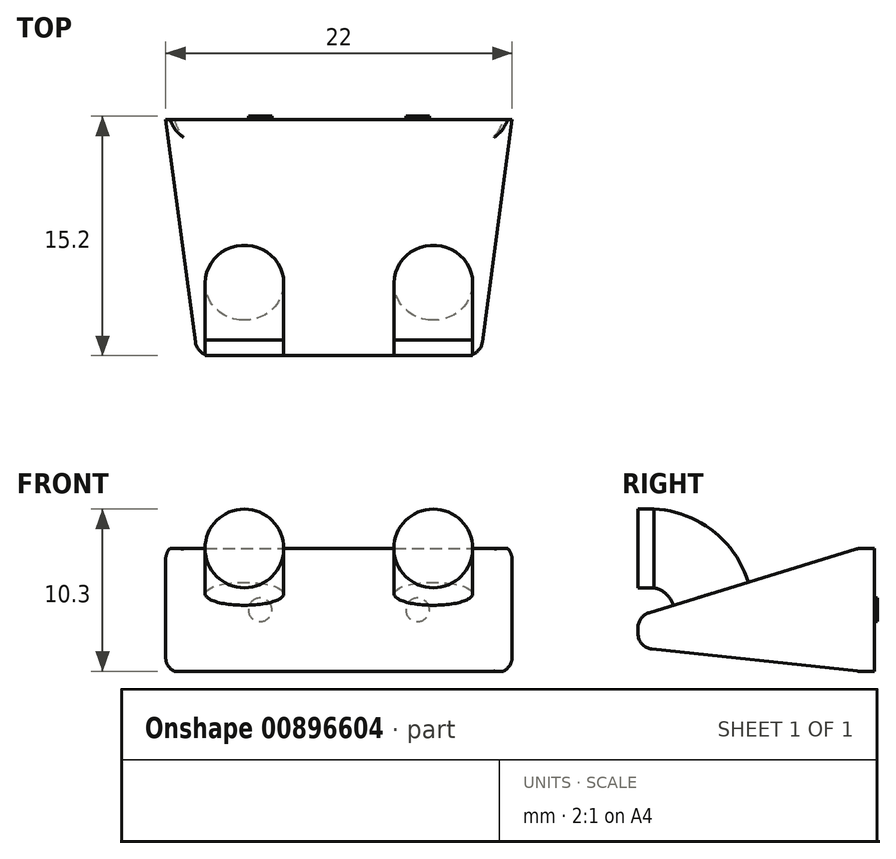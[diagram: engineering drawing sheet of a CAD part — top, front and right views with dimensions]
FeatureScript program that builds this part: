
annotation { "Feature Type Name" : "Feature", "Feature Type Description" : "" }
export const myFeature = defineFeature(function(context is Context, id is Id, definition is map)
    precondition{}
    {
        {
            var Q0;
            Q0=qCreatedBy(makeId("Front.planeOp"),FACE);
            var sketch = newSketch(context, id + "F0", { "sketchPlane" : qUnion([Q0])});
            skLineSegment(sketch, "E0.bottom", {"start": v(0, 0) * mm, "end": v(22, 0) * mm});
            skLineSegment(sketch, "E0.top", {"start": v(0, 7.8) * mm, "end": v(22, 7.8) * mm});
            skLineSegment(sketch, "E0.left", {"start": v(0, 0) * mm, "end": v(0, 7.8) * mm});
            skLineSegment(sketch, "E0.right", {"start": v(22, 0) * mm, "end": v(22, 7.8) * mm});
            skCircle(sketch, "E1", {"center": v(6, 3.9) * mm, "radius": 0.75 * mm});
            skCircle(sketch, "E2", {"center": v(16, 3.9) * mm, "radius": 0.75 * mm});
            skSolve(sketch);
        }
        {
            var Q0;
            Q0=makeQuery(id+"F0.imprint","IMPRINT",FACE,{"disambiguationData":[TD([[makeQuery(id+"F0.imprint","IMPRINT",EDGE,{"derivedFrom":sQuery(id+"F0.wireOp",EDGE,"E0.bottom")}),1.0]])]});
            var Q1;
            Q1=makeQuery(id+"F0.imprint","IMPRINT",FACE,{"disambiguationData":[TD([[makeQuery(id+"F0.imprint","IMPRINT",EDGE,{"derivedFrom":sQuery(id+"F0.wireOp",EDGE,"E2")}),1.0]])]});
            var Q2;
            Q2=makeQuery(id+"F0.imprint","IMPRINT",FACE,{"disambiguationData":[TD([[makeQuery(id+"F0.imprint","IMPRINT",EDGE,{"derivedFrom":sQuery(id+"F0.wireOp",EDGE,"E1")}),1.0]])]});
            extrude(context, id + "F1", {"entities" : qUnion([Q0, Q1, Q2]), "depth" : 1 * mm, "offsetDistance" : 25 * mm});
        }
        {
            var Q0;
            Q0=makeQuery(id+"F0.imprint","IMPRINT",FACE,{"disambiguationData":[TD([[makeQuery(id+"F0.imprint","IMPRINT",EDGE,{"derivedFrom":sQuery(id+"F0.wireOp",EDGE,"E2")}),1.0]])]});
            var Q1;
            Q1=makeQuery(id+"F0.imprint","IMPRINT",FACE,{"disambiguationData":[TD([[makeQuery(id+"F0.imprint","IMPRINT",EDGE,{"derivedFrom":sQuery(id+"F0.wireOp",EDGE,"E1")}),1.0]])]});
            extrude(context, id + "F2", {"entities" : qUnion([Q0, Q1]), "operationType" : NewBodyOperationType.ADD, "oppositeDirection" : true, "depth" : .2 * mm, "offsetDistance" : 25 * mm});
        }
        {
            var Q0;
            Q0=makeQuery(id+"F1.opExtrude","SWEPT_FACE",FACE,{"disambiguationData":[OSD([sQuery(id+"F0.wireOp",EDGE,"E0.right")])]});
            var sketch = newSketch(context, id + "F3", { "sketchPlane" : qUnion([Q0])});
            skLineSegment(sketch, "E3", {"start": v(-1, 0) * mm, "end": v(-15, 1.5) * mm});
            skLineSegment(sketch, "E4", {"start": v(-15, 1.5) * mm, "end": v(-15, 3.5) * mm});
            skLineSegment(sketch, "E5", {"start": v(-15, 3.5) * mm, "end": v(-1, 7.8) * mm});
            skSolve(sketch);
        }
        {
            var Q0;
            Q0 = qSketchRegion(id + "F3", true);
            var Q1;
            Q1=makeQuery(id+"F3.imprint","IMPRINT",FACE,{"disambiguationData":[TD([[makeQuery(id+"F3.imprint","IMPRINT",EDGE,{"derivedFrom":sQuery(id+"F3.wireOp",EDGE,"E3")}),-1.0]])]});
            extrude(context, id + "F4", {"entities" : qUnion([Q0, Q1]), "operationType" : NewBodyOperationType.ADD, "oppositeDirection" : true, "depth" : 22 * mm, "offsetDistance" : 25 * mm});
        }
        {
            var Q0;
            Q0=makeQuery(id+"F4.opExtrude","CAP_EDGE",EDGE,{"disambiguationData":[OSD([sQuery(id+"F3.wireOp",EDGE,"E4")])],"isStart":true});
            var Q1;
            Q1=makeQuery(id+"F4.opExtrude","CAP_EDGE",EDGE,{"disambiguationData":[OSD([sQuery(id+"F3.wireOp",EDGE,"E4")])],"isStart":false});
            chamfer(context, id + "F5", {"entities" : qUnion([Q0, Q1]), "chamferType" : ChamferType.TWO_OFFSETS, "width1" : 2 * mm, "oppositeDirection" : false, "width2" : 15 * mm, "tangentPropagation" : true});
        }
        {
            var Q0;
            Q0=makeQuery(id+"F4.opExtrude","SWEPT_EDGE",EDGE,{"disambiguationData":[OSD([sQuery(id+"F3.wireOp",EDGE,"E4"),sQuery(id+"F3.wireOp",EDGE,"E5")])]});
            var Q1;
            Q1=makeQuery(id+"F4.opExtrude","SWEPT_EDGE",EDGE,{"disambiguationData":[OSD([sQuery(id+"F3.wireOp",EDGE,"E3"),sQuery(id+"F3.wireOp",EDGE,"E4")])]});
            var Q2;
            Q2=makeQuery(id+"F5.opChamfer","BLEND_EDGE",EDGE,{"blendedFrom":[makeQuery(id+"F4.opExtrude","CAP_EDGE",EDGE,{"disambiguationData":[OSD([sQuery(id+"F3.wireOp",EDGE,"E4")])],"isStart":false}),makeQuery(id+"F4.opExtrude","SWEPT_FACE",FACE,{"disambiguationData":[OSD([sQuery(id+"F3.wireOp",EDGE,"E5")])]})],"blendedInto":[makeQuery(id+"F4.opExtrude","SWEPT_FACE",FACE,{"disambiguationData":[OSD([sQuery(id+"F3.wireOp",EDGE,"E5")])]})]});
            var Q3;
            Q3=makeQuery(id+"F5.opChamfer","BLEND_EDGE",EDGE,{"blendedFrom":[makeQuery(id+"F4.opExtrude","CAP_EDGE",EDGE,{"disambiguationData":[OSD([sQuery(id+"F3.wireOp",EDGE,"E4")])],"isStart":false}),makeQuery(id+"F4.opExtrude","SWEPT_FACE",FACE,{"disambiguationData":[OSD([sQuery(id+"F3.wireOp",EDGE,"E3")])]})],"blendedInto":[makeQuery(id+"F4.opExtrude","SWEPT_FACE",FACE,{"disambiguationData":[OSD([sQuery(id+"F3.wireOp",EDGE,"E3")])]})]});
            var Q4;
            Q4=makeQuery(id+"F5.opChamfer","BLEND_EDGE",EDGE,{"blendedFrom":[makeQuery(id+"F4.opExtrude","CAP_EDGE",EDGE,{"disambiguationData":[OSD([sQuery(id+"F3.wireOp",EDGE,"E4")])],"isStart":true}),makeQuery(id+"F4.opExtrude","SWEPT_FACE",FACE,{"disambiguationData":[OSD([sQuery(id+"F3.wireOp",EDGE,"E5")])]})],"blendedInto":[makeQuery(id+"F4.opExtrude","SWEPT_FACE",FACE,{"disambiguationData":[OSD([sQuery(id+"F3.wireOp",EDGE,"E5")])]})]});
            var Q5;
            Q5=makeQuery(id+"F5.opChamfer","BLEND_EDGE",EDGE,{"blendedFrom":[makeQuery(id+"F4.opExtrude","CAP_EDGE",EDGE,{"disambiguationData":[OSD([sQuery(id+"F3.wireOp",EDGE,"E4")])],"isStart":true}),makeQuery(id+"F4.opExtrude","SWEPT_FACE",FACE,{"disambiguationData":[OSD([sQuery(id+"F3.wireOp",EDGE,"E3")])]})],"blendedInto":[makeQuery(id+"F4.opExtrude","SWEPT_FACE",FACE,{"disambiguationData":[OSD([sQuery(id+"F3.wireOp",EDGE,"E3")])]})]});
            var Q6;
            {var subQ0=sQuery(id+"F3.wireOp",EDGE,"E4");Q6=makeQuery(id+"F5.opChamfer","BLEND_EDGE",EDGE,{"blendedFrom":[makeQuery(id+"F4.opExtrude","CAP_EDGE",EDGE,{"disambiguationData":[OSD([subQ0])],"isStart":true}),makeQuery(id+"F4.opExtrude","SWEPT_FACE",FACE,{"disambiguationData":[OSD([subQ0])]})],"blendedInto":[makeQuery(id+"F4.opExtrude","SWEPT_FACE",FACE,{"disambiguationData":[OSD([subQ0])]})]});}
            var Q7;
            {var subQ0=sQuery(id+"F3.wireOp",EDGE,"E4");Q7=makeQuery(id+"F5.opChamfer","BLEND_EDGE",EDGE,{"blendedFrom":[makeQuery(id+"F4.opExtrude","CAP_EDGE",EDGE,{"disambiguationData":[OSD([subQ0])],"isStart":false}),makeQuery(id+"F4.opExtrude","SWEPT_FACE",FACE,{"disambiguationData":[OSD([subQ0])]})],"blendedInto":[makeQuery(id+"F4.opExtrude","SWEPT_FACE",FACE,{"disambiguationData":[OSD([subQ0])]})]});}
            var Q8;
            {var subQ0=sQuery(id+"F0.wireOp",EDGE,"E0.bottom");Q8=makeQuery(id+"F4.boolean.opBoolean","MERGE",EDGE,{"derivedFrom":[makeQuery(id+"F1.opExtrude","CAP_EDGE",EDGE,{"disambiguationData":[OSD([subQ0])],"isStart":false}),makeQuery(id+"F4.opExtrude","SWEPT_EDGE",EDGE,{"disambiguationData":[OSD([subQ0,sQuery(id+"F0.wireOp",EDGE,"E0.right"),sQuery(id+"F3.wireOp",EDGE,"E3")])]})]});}
            var Q9;
            {var subQ0=sQuery(id+"F0.wireOp",EDGE,"E0.top");Q9=makeQuery(id+"F4.boolean.opBoolean","MERGE",EDGE,{"derivedFrom":[makeQuery(id+"F1.opExtrude","CAP_EDGE",EDGE,{"disambiguationData":[OSD([subQ0])],"isStart":false}),makeQuery(id+"F4.opExtrude","SWEPT_EDGE",EDGE,{"disambiguationData":[OSD([subQ0,sQuery(id+"F0.wireOp",EDGE,"E0.right"),sQuery(id+"F3.wireOp",EDGE,"E5")])]})]});}
            fillet(context, id + "F6", {"entities" : qUnion([Q0, Q1, Q2, Q3, Q4, Q5, Q6, Q7, Q8, Q9]), "radius" : 1 * mm, "tangentPropagation" : true, "allowEdgeOverflow" : false});
        }
        {
            var Q0;
            Q0=makeQuery(id+"F4.opExtrude","SWEPT_FACE",FACE,{"disambiguationData":[OSD([sQuery(id+"F3.wireOp",EDGE,"E4")])]});
            var sketch = newSketch(context, id + "F7", { "sketchPlane" : qUnion([Q0])});
            skCircle(sketch, "E6", {"center": v(17, 7.8) * mm, "radius": 2.5 * mm});
            skCircle(sketch, "E7", {"center": v(5, 7.8) * mm, "radius": 2.5 * mm});
            skSolve(sketch);
        }
        {
            var Q0;
            Q0=makeQuery(id+"F7.imprint","IMPRINT",FACE,{"disambiguationData":[TD([[makeQuery(id+"F7.imprint","IMPRINT",EDGE,{"derivedFrom":sQuery(id+"F7.wireOp",EDGE,"E6")}),1.0]])]});
            var Q1;
            Q1=makeQuery(id+"F7.imprint","IMPRINT",FACE,{"disambiguationData":[TD([[makeQuery(id+"F7.imprint","IMPRINT",EDGE,{"derivedFrom":sQuery(id+"F7.wireOp",EDGE,"E7")}),1.0]])]});
            extrude(context, id + "F8", {"entities" : qUnion([Q0, Q1]), "oppositeDirection" : true, "depth" : 1 * mm, "offsetDistance" : 25 * mm});
        }
        {
            var Q0;
            Q0=makeQuery(id+"F8.opExtrude","CAP_FACE",FACE,{"disambiguationData":[OSD([sQuery(id+"F7.wireOp",EDGE,"E7")])],"isStart":false});
            var Q1;
            Q1=makeQuery(id+"F8.opExtrude","CAP_FACE",FACE,{"disambiguationData":[OSD([sQuery(id+"F7.wireOp",EDGE,"E6")])],"isStart":false});
            var Q2;
            {var subQ0=sQuery(id+"F3.wireOp",EDGE,"E5");Q2=makeQuery(id+"F6.opFillet","BLEND_EDGE",EDGE,{"blendedFrom":[makeQuery(id+"F4.opExtrude","SWEPT_EDGE",EDGE,{"disambiguationData":[OSD([sQuery(id+"F3.wireOp",EDGE,"E4"),subQ0])]}),makeQuery(id+"F4.opExtrude","SWEPT_FACE",FACE,{"disambiguationData":[OSD([subQ0])]})],"blendedInto":[makeQuery(id+"F4.opExtrude","SWEPT_FACE",FACE,{"disambiguationData":[OSD([subQ0])]})]});}
            revolve(context, id + "F9", {"operationType" : NewBodyOperationType.ADD, "surfaceOperationType" : NewSurfaceOperationType.NEW, "entities" : qUnion([Q0, Q1]), "axis" : qUnion([Q2]), "revolveType" : RevolveType.ONE_DIRECTION, "oppositeDirection" : true, "angle" : 72.93 * degree});
        }
    });
